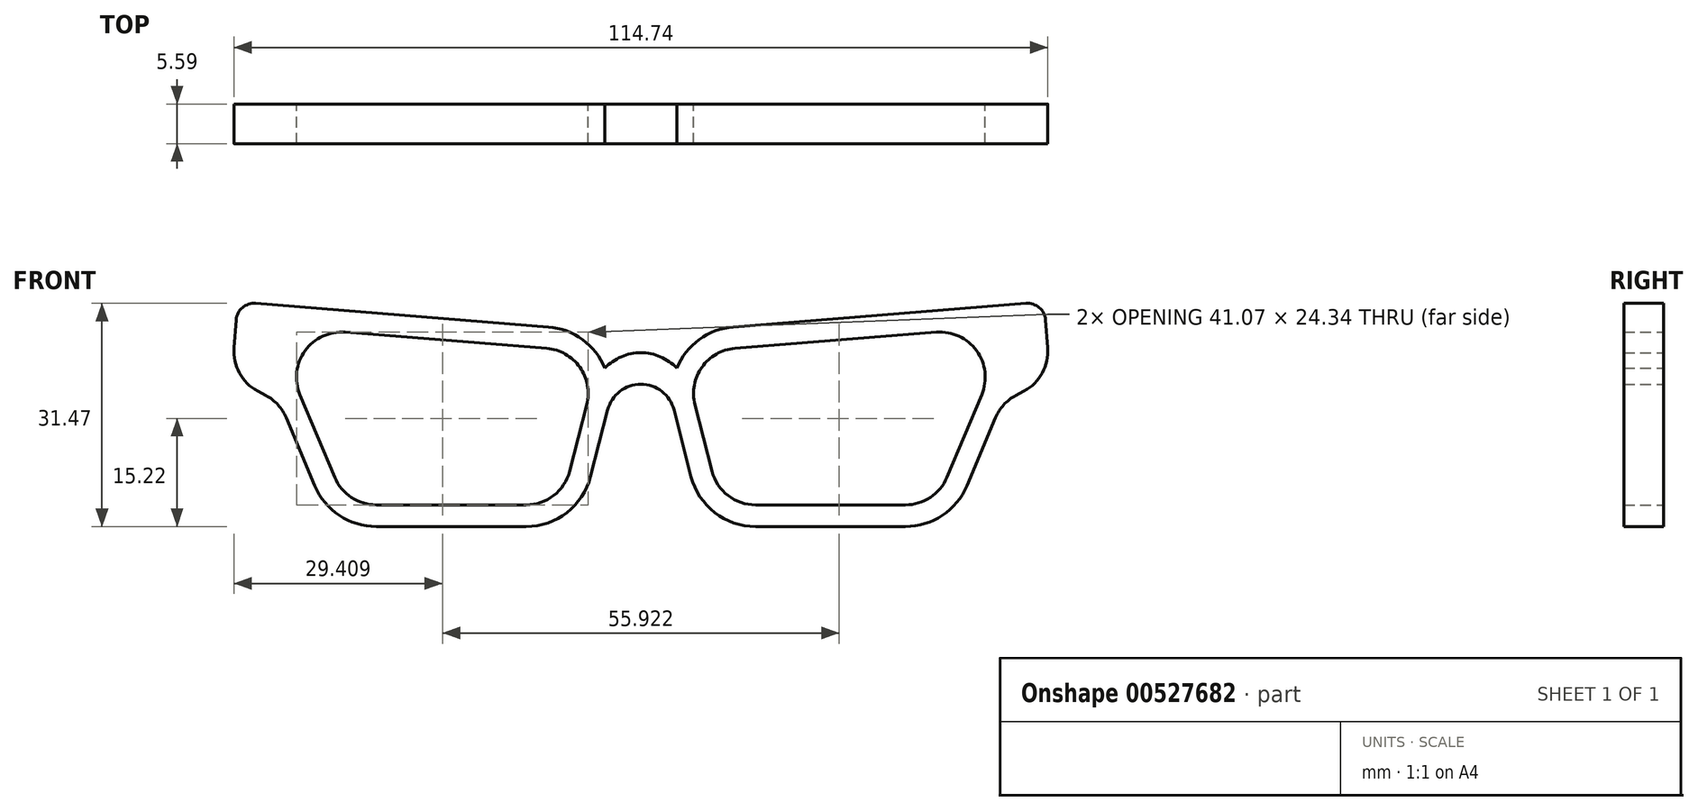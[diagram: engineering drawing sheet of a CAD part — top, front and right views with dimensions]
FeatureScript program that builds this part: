
annotation { "Feature Type Name" : "Feature", "Feature Type Description" : "" }
export const myFeature = defineFeature(function(context is Context, id is Id, definition is map)
    precondition{}
    {
        {
            var Q0;
            Q0=qCreatedBy(makeId("Front.planeOp"),FACE);
            var sketch = newSketch(context, id + "F0", { "sketchPlane" : qUnion([Q0])});
            skLineSegment(sketch, "E0", {"start": v(13.27, 12.27) * mm, "end": v(41.68, 14.55) * mm});
            skLineSegment(sketch, "E1", {"start": v(48.04, 5.76) * mm, "end": v(43.14, -5.9) * mm});
            skLineSegment(sketch, "E2", {"start": v(37.29, -9.8) * mm, "end": v(16.18, -9.8) * mm});
            skLineSegment(sketch, "E3", {"start": v(10.03, -5.02) * mm, "end": v(7.62, 4.36) * mm});
            skPoint(sketch, "E4.visualSharp", {"position": v(5.75, 11.66) * mm});
            skArc(sketch, "E4.filletArc", {"start": v(13.27, 12.27) * mm, "mid": v(8.6, 9.63) * mm, "end": v(7.62, 4.36) * mm});
            skPoint(sketch, "E5.visualSharp", {"position": v(52.08, 15.39) * mm});
            skArc(sketch, "E5.filletArc", {"start": v(48.04, 5.76) * mm, "mid": v(47.33, 11.95) * mm, "end": v(41.68, 14.55) * mm});
            skPoint(sketch, "E6.visualSharp", {"position": v(41.5, -9.8) * mm});
            skArc(sketch, "E6.filletArc", {"start": v(37.29, -9.8) * mm, "mid": v(40.8, -8.73) * mm, "end": v(43.14, -5.9) * mm});
            skPoint(sketch, "E7.visualSharp", {"position": v(11.26, -9.8) * mm});
            skArc(sketch, "E7.filletArc", {"start": v(10.03, -5.02) * mm, "mid": v(12.3, -8.46) * mm, "end": v(16.18, -9.8) * mm});
            skArc(sketch, "E8.0", {"start": v(13.02, 15.3) * mm, "mid": v(8.22, 13.52) * mm, "end": v(5.07, 9.48) * mm});
            skLineSegment(sketch, "E8.1", {"start": v(7.08, -5.78) * mm, "end": v(4.67, 3.6) * mm});
            skLineSegment(sketch, "E8.2", {"start": v(13.02, 15.3) * mm, "end": v(53.3, 18.54) * mm});
            skArc(sketch, "E8.3", {"start": v(7.08, -5.78) * mm, "mid": v(10.42, -10.87) * mm, "end": v(16.18, -12.84) * mm});
            skLineSegment(sketch, "E8.5", {"start": v(49.97, 2.5) * mm, "end": v(45.95, -7.08) * mm});
            skArc(sketch, "E8.6", {"start": v(37.29, -12.84) * mm, "mid": v(42.49, -11.27) * mm, "end": v(45.95, -7.08) * mm});
            skLineSegment(sketch, "E8.7", {"start": v(37.29, -12.84) * mm, "end": v(16.18, -12.84) * mm});
            skLineSegment(sketch, "E9", {"start": v(53.3, 18.54) * mm, "end": v(54.3, 18.62) * mm});
            skLineSegment(sketch, "E10", {"start": v(57.03, 16.3) * mm, "end": v(57.35, 12.37) * mm});
            skLineSegment(sketch, "E11", {"start": v(54, 6.25) * mm, "end": v(52.85, 5.64) * mm});
            skPoint(sketch, "E12.visualSharp", {"position": v(50.85, 4.58) * mm});
            skArc(sketch, "E12.filletArc", {"start": v(52.85, 5.64) * mm, "mid": v(51.14, 4.32) * mm, "end": v(49.97, 2.5) * mm});
            skPoint(sketch, "E13.visualSharp", {"position": v(57.68, 8.2) * mm});
            skArc(sketch, "E13.filletArc", {"start": v(54, 6.25) * mm, "mid": v(56.59, 8.8) * mm, "end": v(57.35, 12.37) * mm});
            skPoint(sketch, "E14.visualSharp", {"position": v(56.83, 18.83) * mm});
            skArc(sketch, "E14.filletArc", {"start": v(57.03, 16.3) * mm, "mid": v(56.14, 18.03) * mm, "end": v(54.3, 18.62) * mm});
            skArc(sketch, "E15.MirrorCS", {"start": v(-57.03, 16.3) * mm, "mid": v(-56.14, 18.03) * mm, "end": v(-54.3, 18.62) * mm});
            skLineSegment(sketch, "E16.MirrorCS", {"start": v(-57.03, 16.3) * mm, "end": v(-57.35, 12.37) * mm});
            skLineSegment(sketch, "E17.MirrorCS", {"start": v(-54, 6.25) * mm, "end": v(-52.85, 5.64) * mm});
            skArc(sketch, "E18.MirrorCS", {"start": v(-52.85, 5.64) * mm, "mid": v(-51.14, 4.32) * mm, "end": v(-49.97, 2.5) * mm});
            skArc(sketch, "E19.MirrorCS", {"start": v(-54, 6.25) * mm, "mid": v(-56.59, 8.8) * mm, "end": v(-57.35, 12.37) * mm});
            skArc(sketch, "E20.MirrorCS", {"start": v(-37.29, -9.8) * mm, "mid": v(-40.8, -8.73) * mm, "end": v(-43.14, -5.9) * mm});
            skArc(sketch, "E21.MirrorCS", {"start": v(-10.03, -5.02) * mm, "mid": v(-12.3, -8.46) * mm, "end": v(-16.18, -9.8) * mm});
            skArc(sketch, "E22.MirrorCS", {"start": v(-7.08, -5.78) * mm, "mid": v(-10.42, -10.87) * mm, "end": v(-16.18, -12.84) * mm});
            skPoint(sketch, "E23.MirrorP", {"position": v(-5.75, 11.66) * mm});
            skArc(sketch, "E24.MirrorCS", {"start": v(-37.29, -12.84) * mm, "mid": v(-42.49, -11.27) * mm, "end": v(-45.95, -7.08) * mm});
            skLineSegment(sketch, "E25.MirrorCS", {"start": v(-37.29, -12.84) * mm, "end": v(-16.18, -12.84) * mm});
            skLineSegment(sketch, "E26.MirrorCS", {"start": v(-53.3, 18.54) * mm, "end": v(-54.3, 18.62) * mm});
            skLineSegment(sketch, "E27.MirrorCS", {"start": v(-13.27, 12.27) * mm, "end": v(-41.68, 14.55) * mm});
            skLineSegment(sketch, "E28.MirrorCS", {"start": v(-48.04, 5.76) * mm, "end": v(-43.14, -5.9) * mm});
            skLineSegment(sketch, "E29.MirrorCS", {"start": v(-37.29, -9.8) * mm, "end": v(-16.18, -9.8) * mm});
            skLineSegment(sketch, "E30.MirrorCS", {"start": v(-10.03, -5.02) * mm, "end": v(-7.62, 4.36) * mm});
            skArc(sketch, "E31.MirrorCS", {"start": v(-13.27, 12.27) * mm, "mid": v(-8.6, 9.63) * mm, "end": v(-7.62, 4.36) * mm});
            skArc(sketch, "E32.MirrorCS", {"start": v(-48.04, 5.76) * mm, "mid": v(-47.33, 11.95) * mm, "end": v(-41.68, 14.55) * mm});
            skPoint(sketch, "E33.MirrorP", {"position": v(-11.26, -9.8) * mm});
            skArc(sketch, "E34.MirrorCS", {"start": v(-13.02, 15.3) * mm, "mid": v(-8.22, 13.52) * mm, "end": v(-5.07, 9.48) * mm});
            skLineSegment(sketch, "E35.MirrorCS", {"start": v(-7.08, -5.78) * mm, "end": v(-4.67, 3.6) * mm});
            skLineSegment(sketch, "E36.MirrorCS", {"start": v(-49.97, 2.5) * mm, "end": v(-45.95, -7.08) * mm});
            skLineSegment(sketch, "E37.MirrorCS", {"start": v(-13.02, 15.3) * mm, "end": v(-53.3, 18.54) * mm});
            skPoint(sketch, "E38.MirrorP", {"position": v(-57.68, 8.2) * mm});
            skPoint(sketch, "E39.MirrorP", {"position": v(-56.83, 18.83) * mm});
            skPoint(sketch, "E40.MirrorP", {"position": v(-41.5, -9.8) * mm});
            skPoint(sketch, "E41.MirrorP", {"position": v(-52.08, 15.39) * mm});
            skPoint(sketch, "E42.MirrorP", {"position": v(-50.85, 4.58) * mm});
            skArc(sketch, "E43", {"start": v(5.07, 9.48) * mm, "mid": v(0, 11.66) * mm, "end": v(-5.07, 9.48) * mm});
            skArc(sketch, "E44", {"start": v(4.67, 3.6) * mm, "mid": v(0, 7.22) * mm, "end": v(-4.67, 3.6) * mm});
            skSolve(sketch);
        }
        {
            var Q0;
            Q0=makeQuery(id+"F0.imprint","IMPRINT",FACE,{"disambiguationData":[TD([[makeQuery(id+"F0.imprint","IMPRINT",EDGE,{"derivedFrom":sQuery(id+"F0.wireOp",EDGE,"E0")}),1.0]])]});
            extrude(context, id + "F1", {"entities" : qUnion([Q0]), "depth" : 5.6 * mm, "offsetDistance" : 25.4 * mm});
        }
    });
